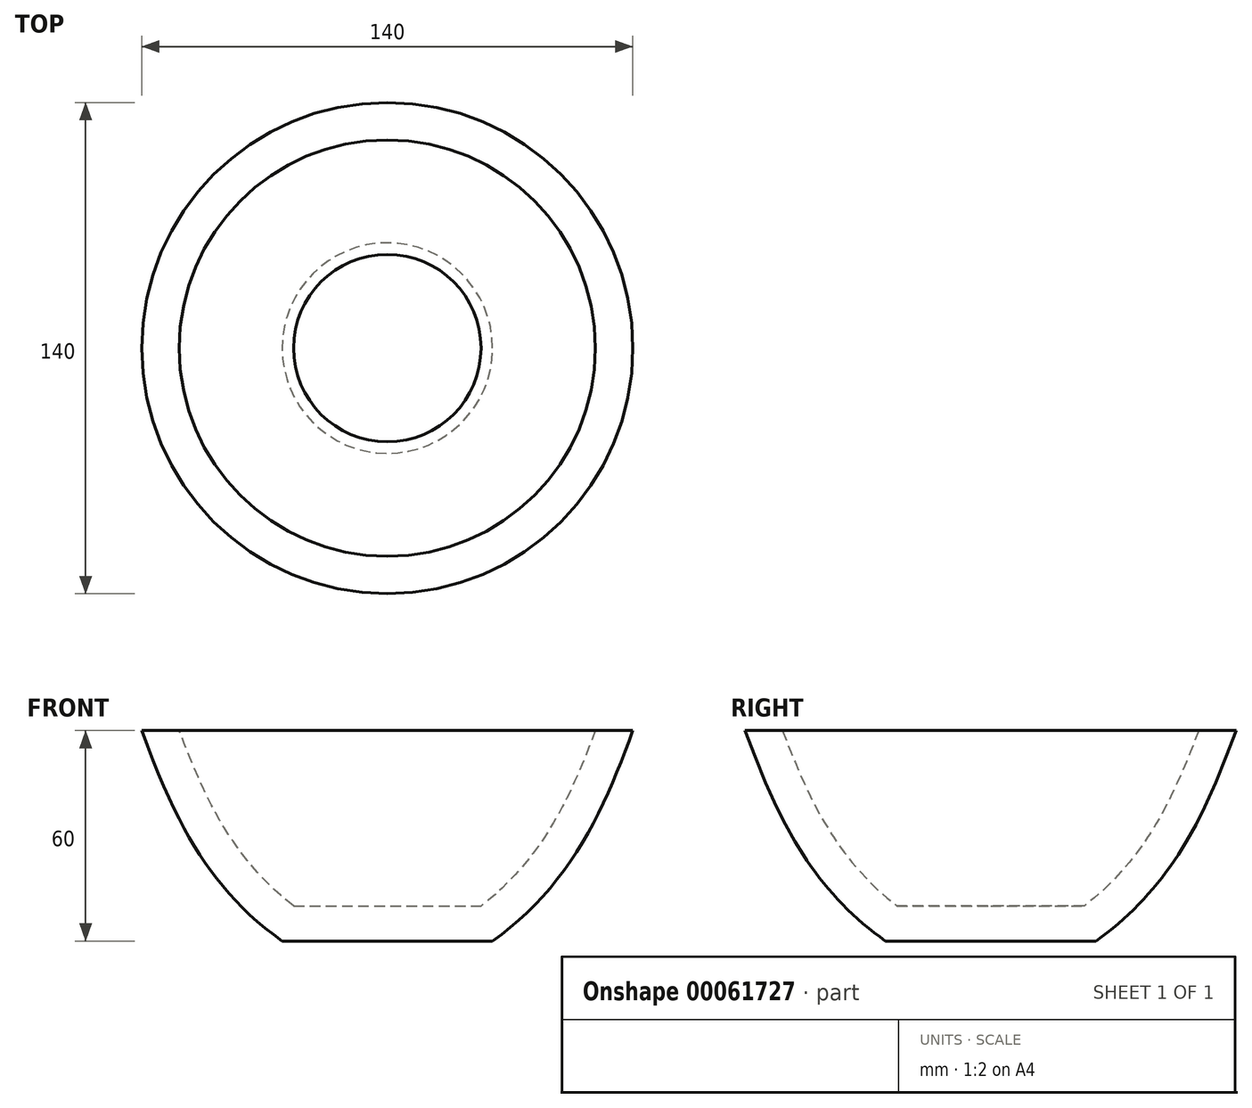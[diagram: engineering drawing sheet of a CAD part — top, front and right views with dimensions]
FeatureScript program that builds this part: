
annotation { "Feature Type Name" : "Feature", "Feature Type Description" : "" }
export const myFeature = defineFeature(function(context is Context, id is Id, definition is map)
    precondition{}
    {
        {
            var Q0;
            Q0=qCreatedBy(makeId("Front.planeOp"),FACE);
            var sketch = newSketch(context, id + "F0", { "sketchPlane" : qUnion([Q0])});
            skLineSegment(sketch, "E0", {"start": v(0, 0) * mm, "end": v(30, 0) * mm});
            skLineSegment(sketch, "E1", {"start": v(0, 60) * mm, "end": v(70, 60) * mm});
            skLineSegment(sketch, "E2", {"start": v(0, 0) * mm, "end": v(0, 60) * mm});
            skFitSpline(sketch, "E3", {"points": [v(30, 0) * mm, v(51, 21) * mm, v(70, 60) * mm], "startDerivative": vector(58, 41.12) * mm, "endDerivative": vector(38.4, 104.38) * mm});
            skSolve(sketch);
        }
        {
            var Q0;
            Q0=makeQuery(id+"F0.imprint","IMPRINT",FACE,{"disambiguationData":[TD([[makeQuery(id+"F0.imprint","IMPRINT",EDGE,{"derivedFrom":sQuery(id+"F0.wireOp",EDGE,"E0")}),1.0]])]});
            var Q1;
            Q1=sQuery(id+"F0.wireOp",EDGE,"E2");
            revolve(context, id + "F1", {"entities" : qUnion([Q0]), "axis" : qUnion([Q1]), "revolveType" : RevolveType.FULL});
        }
        {
            var Q0;
            Q0=makeQuery(id+"F1.opRevolve","SWEPT_FACE",FACE,{"disambiguationData":[OSD([sQuery(id+"F0.wireOp",EDGE,"E1")])]});
            shell(context, id + "F2", {"entities" : qUnion([Q0]), "thickness" : 10 * mm});
        }
    });
